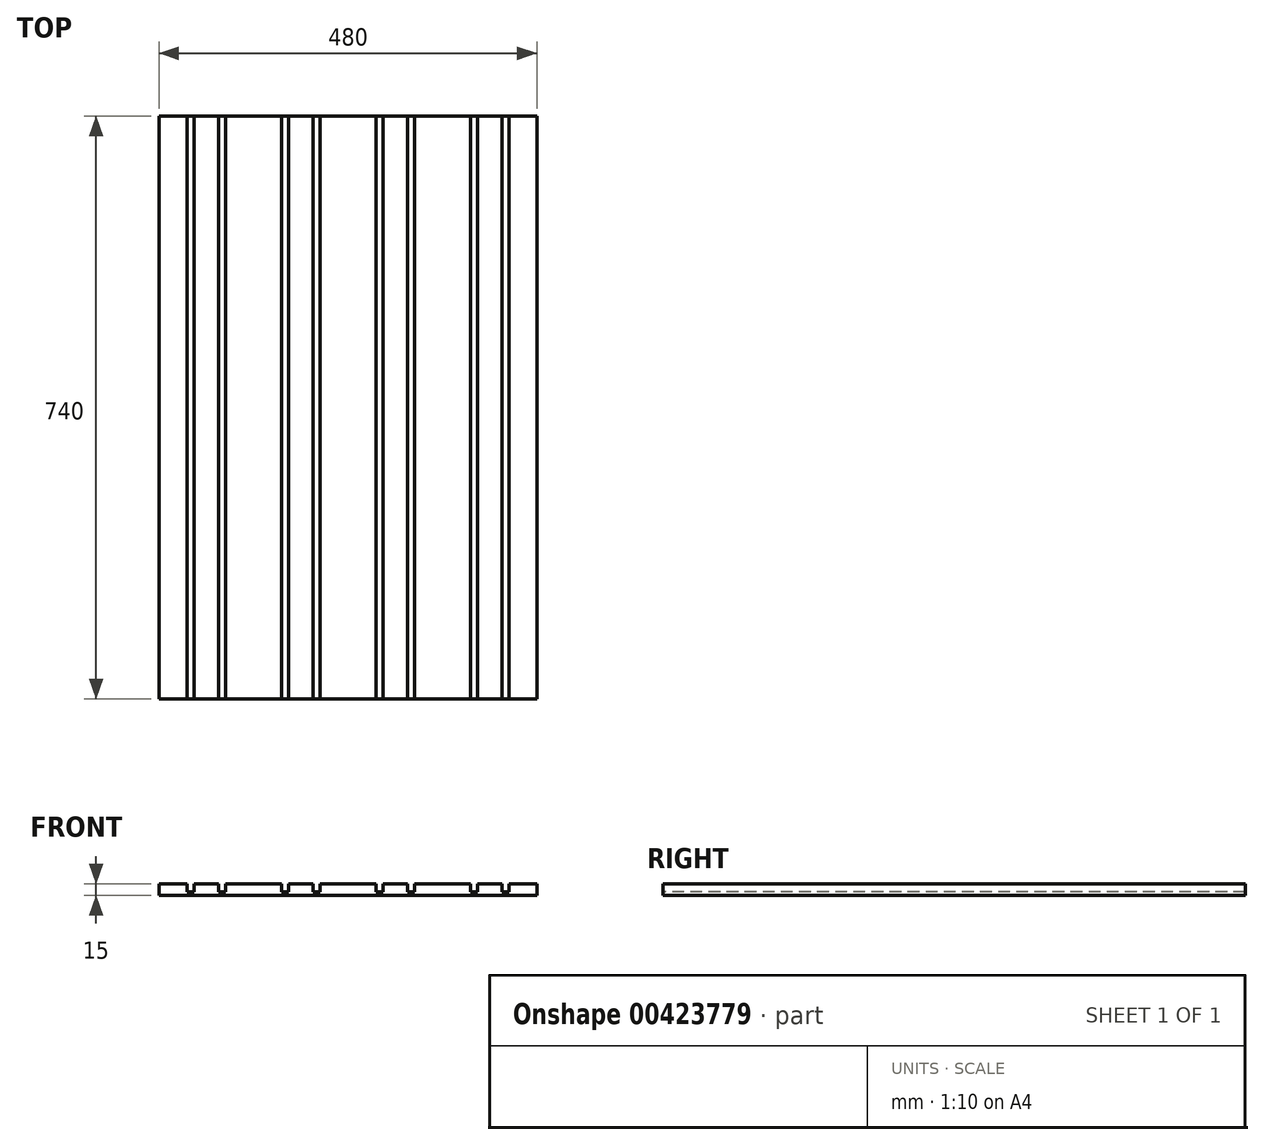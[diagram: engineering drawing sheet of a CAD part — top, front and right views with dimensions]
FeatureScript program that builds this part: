
annotation { "Feature Type Name" : "Feature", "Feature Type Description" : "" }
export const myFeature = defineFeature(function(context is Context, id is Id, definition is map)
    precondition{}
    {
        {
            var Q0;
            Q0=qCreatedBy(makeId("Top.planeOp"),FACE);
            var sketch = newSketch(context, id + "F0", { "sketchPlane" : qUnion([Q0])});
            skLineSegment(sketch, "E0.bottom", {"start": v(240, -370) * mm, "end": v(-240, -370) * mm});
            skLineSegment(sketch, "E0.top", {"start": v(240, 370) * mm, "end": v(-240, 370) * mm});
            skLineSegment(sketch, "E0.left", {"start": v(240, -370) * mm, "end": v(240, 370) * mm});
            skLineSegment(sketch, "E0.right", {"start": v(-240, -370) * mm, "end": v(-240, 370) * mm});
            skPoint(sketch, "E0.middle", {"position": v(0, 0) * mm});
            skLineSegment(sketch, "E1", {"start": v(0, 370) * mm, "end": v(0, -370) * mm});
            skLineSegment(sketch, "E2.1.0.0", {"start": v(35.5, 370) * mm, "end": v(35.5, -370) * mm});
            skLineSegment(sketch, "E2.2.0.0", {"start": v(44.5, 370) * mm, "end": v(44.5, -370) * mm});
            skLineSegment(sketch, "E2.3.0.0", {"start": v(75.5, 370) * mm, "end": v(75.5, -370) * mm});
            skLineSegment(sketch, "E2.4.0.0", {"start": v(84.5, 370) * mm, "end": v(84.5, -370) * mm});
            skLineSegment(sketch, "E2.5.0.0", {"start": v(155.5, 370) * mm, "end": v(155.5, -370) * mm});
            skLineSegment(sketch, "E2.6.0.0", {"start": v(164.5, 370) * mm, "end": v(164.5, -370) * mm});
            skLineSegment(sketch, "E2.7.0.0", {"start": v(195.5, 370) * mm, "end": v(195.5, -370) * mm});
            skLineSegment(sketch, "E2.8.0.0", {"start": v(204.5, 370) * mm, "end": v(204.5, -370) * mm});
            skLineSegment(sketch, "E2.direction1", {"start": v(0, -370) * mm, "end": v(35.5, -370) * mm, "construction": true});
            skSolve(sketch);
        }
        {
            var Q0;
            {var subQ0=sQuery(id+"F0.wireOp",EDGE,"E2.6.0.0");Q0=makeQuery(id+"F0.imprint","IMPRINT",FACE,{"disambiguationData":[TD([[makeQuery(id+"F0.imprint","IMPRINT",EDGE,{"derivedFrom":subQ0}),1.0]])]});}
            var Q1;
            {var subQ0=sQuery(id+"F0.wireOp",EDGE,"E2.5.0.0");Q1=makeQuery(id+"F0.imprint","IMPRINT",FACE,{"disambiguationData":[TD([[makeQuery(id+"F0.imprint","IMPRINT",EDGE,{"derivedFrom":subQ0}),1.0]])]});}
            var Q2;
            {var subQ0=sQuery(id+"F0.wireOp",EDGE,"E2.7.0.0");Q2=makeQuery(id+"F0.imprint","IMPRINT",FACE,{"disambiguationData":[TD([[makeQuery(id+"F0.imprint","IMPRINT",EDGE,{"derivedFrom":subQ0}),1.0]])]});}
            var Q3;
            {var subQ0=sQuery(id+"F0.wireOp",EDGE,"E2.4.0.0");Q3=makeQuery(id+"F0.imprint","IMPRINT",FACE,{"disambiguationData":[TD([[makeQuery(id+"F0.imprint","IMPRINT",EDGE,{"derivedFrom":subQ0}),1.0]])]});}
            var Q4;
            {var subQ0=sQuery(id+"F0.wireOp",EDGE,"E2.3.0.0");Q4=makeQuery(id+"F0.imprint","IMPRINT",FACE,{"disambiguationData":[TD([[makeQuery(id+"F0.imprint","IMPRINT",EDGE,{"derivedFrom":subQ0}),1.0]])]});}
            var Q5;
            {var subQ0=sQuery(id+"F0.wireOp",EDGE,"E2.2.0.0");Q5=makeQuery(id+"F0.imprint","IMPRINT",FACE,{"disambiguationData":[TD([[makeQuery(id+"F0.imprint","IMPRINT",EDGE,{"derivedFrom":subQ0}),1.0]])]});}
            var Q6;
            {var subQ0=sQuery(id+"F0.wireOp",EDGE,"E2.1.0.0");Q6=makeQuery(id+"F0.imprint","IMPRINT",FACE,{"disambiguationData":[TD([[makeQuery(id+"F0.imprint","IMPRINT",EDGE,{"derivedFrom":subQ0}),1.0]])]});}
            var Q7;
            {var subQ0=sQuery(id+"F0.wireOp",EDGE,"E0.left");Q7=makeQuery(id+"F0.imprint","IMPRINT",FACE,{"disambiguationData":[TD([[makeQuery(id+"F0.imprint","IMPRINT",EDGE,{"derivedFrom":subQ0}),1.0]])]});}
            var Q8;
            {var subQ0=sQuery(id+"F0.wireOp",EDGE,"E1");Q8=makeQuery(id+"F0.imprint","IMPRINT",FACE,{"disambiguationData":[TD([[makeQuery(id+"F0.imprint","IMPRINT",EDGE,{"derivedFrom":subQ0}),1.0]])]});}
            extrude(context, id + "F1", {"entities" : qUnion([Q0, Q1, Q2, Q3, Q4, Q5, Q6, Q7, Q8]), "oppositeDirection" : true, "depth" : 15 * mm});
        }
        {
            var Q0;
            {var subQ0=sQuery(id+"F0.wireOp",EDGE,"E2.1.0.0");Q0=makeQuery(id+"F0.imprint","IMPRINT",FACE,{"disambiguationData":[TD([[makeQuery(id+"F0.imprint","IMPRINT",EDGE,{"derivedFrom":subQ0}),1.0]])]});}
            var Q1;
            {var subQ0=sQuery(id+"F0.wireOp",EDGE,"E2.3.0.0");Q1=makeQuery(id+"F0.imprint","IMPRINT",FACE,{"disambiguationData":[TD([[makeQuery(id+"F0.imprint","IMPRINT",EDGE,{"derivedFrom":subQ0}),1.0]])]});}
            var Q2;
            {var subQ0=sQuery(id+"F0.wireOp",EDGE,"E2.5.0.0");Q2=makeQuery(id+"F0.imprint","IMPRINT",FACE,{"disambiguationData":[TD([[makeQuery(id+"F0.imprint","IMPRINT",EDGE,{"derivedFrom":subQ0}),1.0]])]});}
            var Q3;
            {var subQ0=sQuery(id+"F0.wireOp",EDGE,"E2.7.0.0");Q3=makeQuery(id+"F0.imprint","IMPRINT",FACE,{"disambiguationData":[TD([[makeQuery(id+"F0.imprint","IMPRINT",EDGE,{"derivedFrom":subQ0}),1.0]])]});}
            extrude(context, id + "F2", {"entities" : qUnion([Q0, Q1, Q2, Q3]), "operationType" : NewBodyOperationType.REMOVE, "oppositeDirection" : true, "depth" : 10 * mm});
        }
        {
            var Q0;
            Q0=makeQuery(id+"F1.opExtrude","SWEPT_BODY",BODY,{"disambiguationData":[OSD([sQuery(id+"F0.wireOp",EDGE,"E0.bottom"),sQuery(id+"F0.wireOp",EDGE,"E0.top"),sQuery(id+"F0.wireOp",EDGE,"E0.left"),sQuery(id+"F0.wireOp",EDGE,"E1")])]});
            var Q1;
            Q1=makeQuery(id+"F1.opExtrude","SWEPT_FACE",FACE,{"disambiguationData":[OSD([sQuery(id+"F0.wireOp",EDGE,"E1")])]});
            mirror(context, id + "F3", {"operationType" : NewBodyOperationType.ADD, "entities" : qUnion([Q0]), "mirrorPlane" : qUnion([Q1])});
        }
    });
